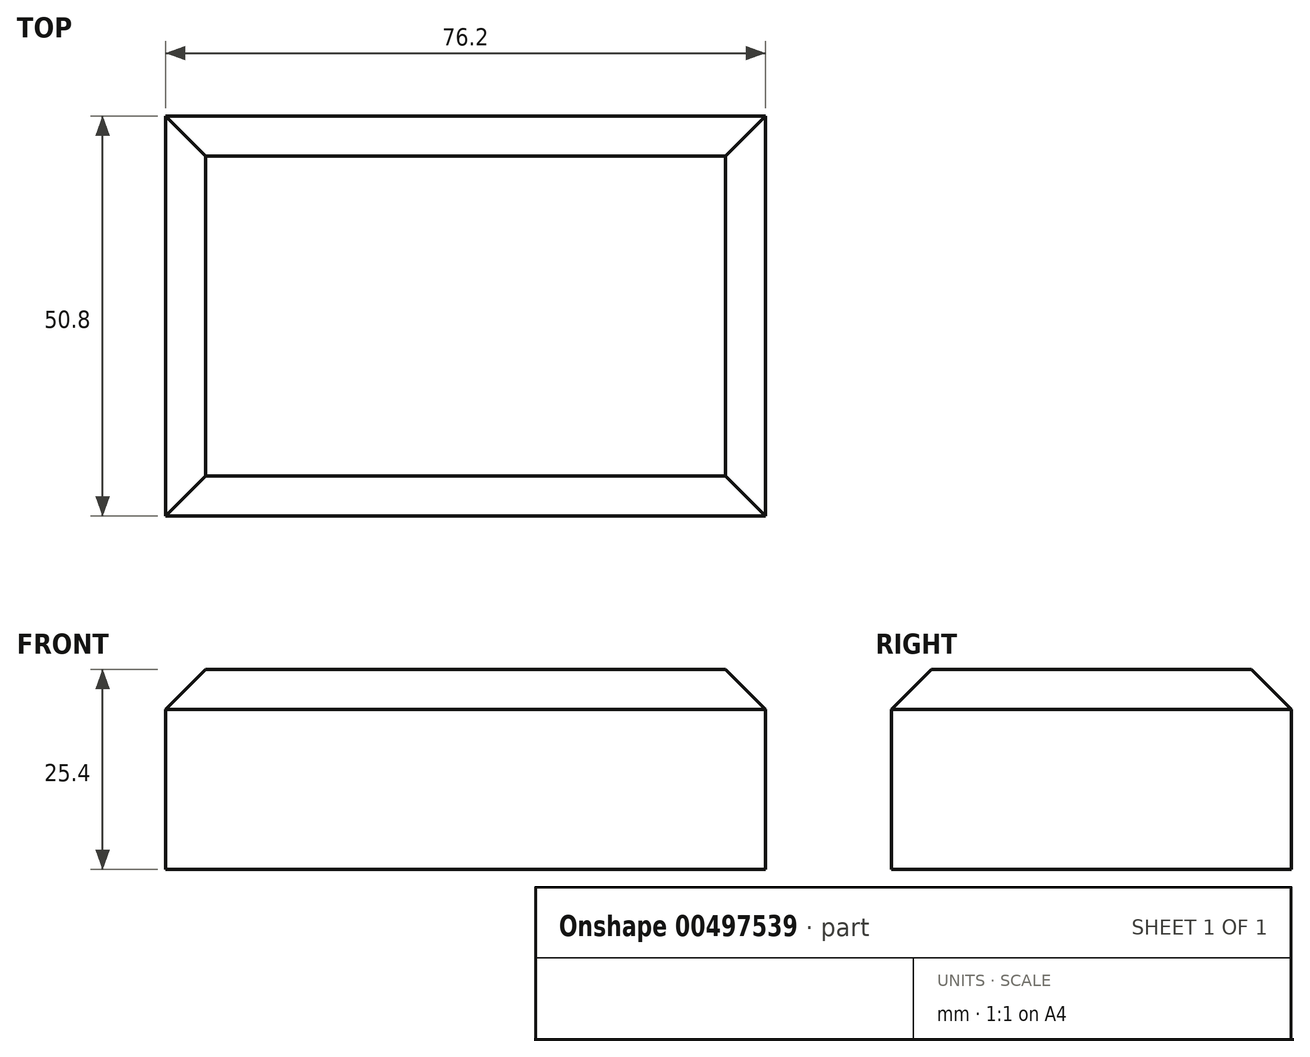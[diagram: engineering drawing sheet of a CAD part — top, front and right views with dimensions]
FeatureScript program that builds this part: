
annotation { "Feature Type Name" : "Feature", "Feature Type Description" : "" }
export const myFeature = defineFeature(function(context is Context, id is Id, definition is map)
    precondition{}
    {
        {
            var Q0;
            Q0=qCreatedBy(makeId("Top.planeOp"),FACE);
            var sketch = newSketch(context, id + "F0", { "sketchPlane" : qUnion([Q0])});
            skLineSegment(sketch, "E0.bottom", {"start": v(38.1, 25.4) * mm, "end": v(-38.1, 25.4) * mm});
            skLineSegment(sketch, "E0.top", {"start": v(38.1, -25.4) * mm, "end": v(-38.1, -25.4) * mm});
            skLineSegment(sketch, "E0.left", {"start": v(38.1, 25.4) * mm, "end": v(38.1, -25.4) * mm});
            skLineSegment(sketch, "E0.right", {"start": v(-38.1, 25.4) * mm, "end": v(-38.1, -25.4) * mm});
            skPoint(sketch, "E0.middle", {"position": v(0, 0) * mm});
            skSolve(sketch);
        }
        {
            var Q0;
            Q0 = qSketchRegion(id + "F0", true);
            extrude(context, id + "F1", {"entities" : qUnion([Q0]), "depth" : 25.4 * mm});
        }
        {
            var Q0;
            Q0=makeQuery(id+"F1.opExtrude","CAP_EDGE",EDGE,{"disambiguationData":[OSD([sQuery(id+"F0.wireOp",EDGE,"E0.right")])],"isStart":false});
            var Q1;
            Q1=makeQuery(id+"F1.opExtrude","CAP_EDGE",EDGE,{"disambiguationData":[OSD([sQuery(id+"F0.wireOp",EDGE,"E0.top")])],"isStart":false});
            var Q2;
            Q2=makeQuery(id+"F1.opExtrude","CAP_EDGE",EDGE,{"disambiguationData":[OSD([sQuery(id+"F0.wireOp",EDGE,"E0.left")])],"isStart":false});
            var Q3;
            Q3=makeQuery(id+"F1.opExtrude","CAP_EDGE",EDGE,{"disambiguationData":[OSD([sQuery(id+"F0.wireOp",EDGE,"E0.bottom")])],"isStart":false});
            chamfer(context, id + "F2", {"entities" : qUnion([Q0, Q1, Q2, Q3]), "width" : 5.08 * mm, "tangentPropagation" : true});
        }
    });
